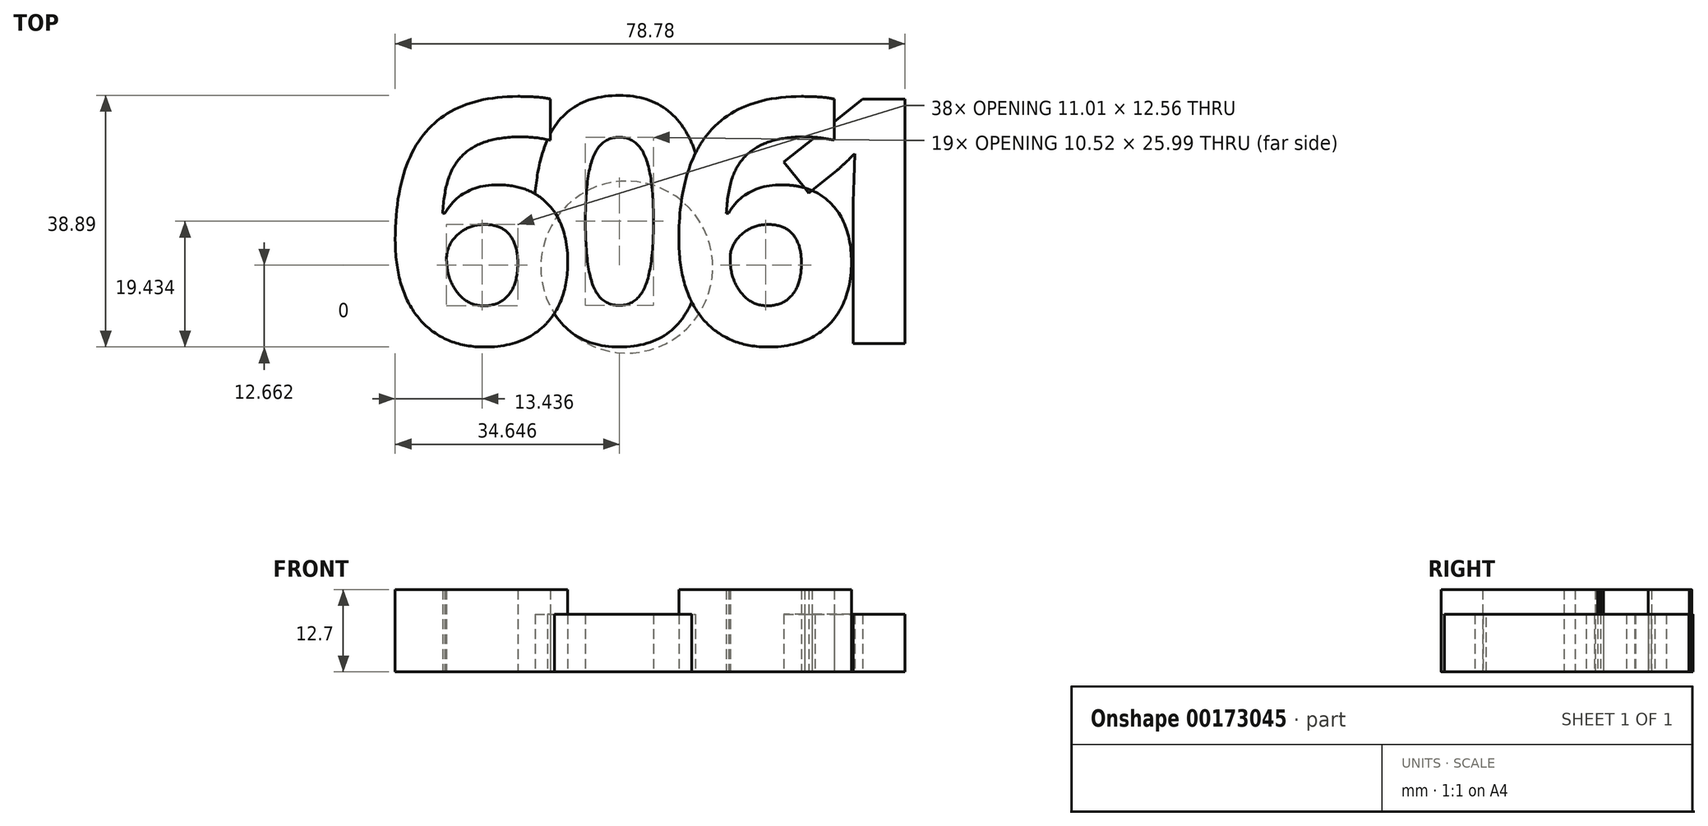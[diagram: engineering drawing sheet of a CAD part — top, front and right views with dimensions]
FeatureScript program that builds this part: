
annotation { "Feature Type Name" : "Feature", "Feature Type Description" : "" }
export const myFeature = defineFeature(function(context is Context, id is Id, definition is map)
    precondition{}
    {
        {
            var Q0;
            Q0=qCreatedBy(makeId("Top.planeOp"),FACE);
            var sketch = newSketch(context, id + "F0", { "sketchPlane" : qUnion([Q0])});
            skLineSegment(sketch, "E0.bottom", {"start": v(0, 0) * mm, "end": v(127, 0) * mm});
            skLineSegment(sketch, "E0.top", {"start": v(0, 50.8) * mm, "end": v(127, 50.8) * mm});
            skLineSegment(sketch, "E0.left", {"start": v(0, 0) * mm, "end": v(0, 50.8) * mm});
            skLineSegment(sketch, "E0.right", {"start": v(127, 0) * mm, "end": v(127, 50.8) * mm});
            skText(sketch, "E1", { "text": "6", "fontName": "OpenSans-Bold.ttf"});
            skText(sketch, "E2", { "text": "0", "fontName": "OpenSans-Bold.ttf"});
            skText(sketch, "E3", { "text": "6", "fontName": "OpenSans-Bold.ttf"});
            skText(sketch, "E4", { "text": "1", "fontName": "OpenSans-Bold.ttf"});
            const initialGuessF0  = {"E1": [0.00635, 0.00635, 1, 0, 0.0381], "E2": [0.02775, 0.00635, 1, 0, 0.0381], "E3": [0.05018, 0.00635, 1, 0, 0.0381], "E4": [0.06513, 0.00635, 1, 0, 0.0381]};
            skSetInitialGuess(sketch, initialGuessF0);
            skSolve(sketch);
        }
        {
            var Q0;
            Q0=makeQuery(id+"F0.imprint","IMPRINT",FACE,{"disambiguationData":[TD([[makeQuery(id+"F0.imprint","IMPRINT",EDGE,{"derivedFrom":sQuery(id+"F0.wireOp",EDGE,"E1.sketch_text.stroke-0")}),-1.0]])]});
            var Q1;
            {var subQ1=sQuery(id+"F0.wireOp",EDGE,"E1.sketch_text.stroke-11");Q1=makeQuery(id+"F0.imprint","IMPRINT",FACE,{"disambiguationData":[TD([[makeQuery(id+"F0.imprint","IMPRINT",EDGE,{"derivedFrom":subQ1}),-1.0]])]});}
            var Q2;
            {var subQ0=sQuery(id+"F0.wireOp",EDGE,"E3.sketch_text.stroke-16");Q2=makeQuery(id+"F0.imprint","IMPRINT",FACE,{"disambiguationData":[TD([[makeQuery(id+"F0.imprint","IMPRINT",EDGE,{"derivedFrom":subQ0}),-1.0]])]});}
            var Q3;
            {var subQ20=sQuery(id+"F0.wireOp",EDGE,"E3.sketch_text.stroke-1");Q3=makeQuery(id+"F0.imprint","IMPRINT",FACE,{"disambiguationData":[TD([[makeQuery(id+"F0.imprint","IMPRINT",EDGE,{"derivedFrom":subQ20}),-1.0]])]});}
            var Q4;
            {var subQ0=sQuery(id+"F0.wireOp",EDGE,"E3.sketch_text.stroke-4");var subQ1=sQuery(id+"F0.wireOp",EDGE,"E3.sketch_text.stroke-3");var subQ2=makeQuery(id+"F0.imprint","INTERSECT",VERTEX,{"derivedFrom":[subQ1,subQ0]});Q4=makeQuery(id+"F0.imprint","IMPRINT",FACE,{"disambiguationData":[TD([[makeQuery(id+"F0.imprint","IMPRINT",EDGE,{"disambiguationData":[TD([[subQ2,1.0]])],"derivedFrom":subQ1}),-1.0]])]});}
            var Q5;
            {var subQ0=sQuery(id+"F0.wireOp",EDGE,"E1.sketch_text.stroke-4");var subQ1=sQuery(id+"F0.wireOp",EDGE,"E1.sketch_text.stroke-3");var subQ2=makeQuery(id+"F0.imprint","INTERSECT",VERTEX,{"derivedFrom":[subQ1,subQ0]});Q5=makeQuery(id+"F0.imprint","IMPRINT",FACE,{"disambiguationData":[TD([[makeQuery(id+"F0.imprint","IMPRINT",EDGE,{"disambiguationData":[TD([[subQ2,1.0]])],"derivedFrom":subQ1}),-1.0]])]});}
            extrude(context, id + "F1", {"entities" : qUnion([Q0, Q1, Q2, Q3, Q4, Q5]), "depth" : 12.7 * mm});
        }
        {
            var Q0;
            {var subQ14=sQuery(id+"F0.wireOp",EDGE,"E1.sketch_text.stroke-11");Q0=makeQuery(id+"F0.imprint","IMPRINT",FACE,{"disambiguationData":[TD([[makeQuery(id+"F0.imprint","IMPRINT",EDGE,{"derivedFrom":subQ14}),1.0]])]});}
            var Q1;
            Q1=makeQuery(id+"F0.imprint","IMPRINT",FACE,{"disambiguationData":[TD([[makeQuery(id+"F0.imprint","IMPRINT",EDGE,{"derivedFrom":sQuery(id+"F0.wireOp",EDGE,"E4.sketch_text.stroke-0")}),-1.0]])]});
            extrude(context, id + "F2", {"entities" : qUnion([Q0, Q1]), "depth" : 8.9 * mm});
        }
    });
